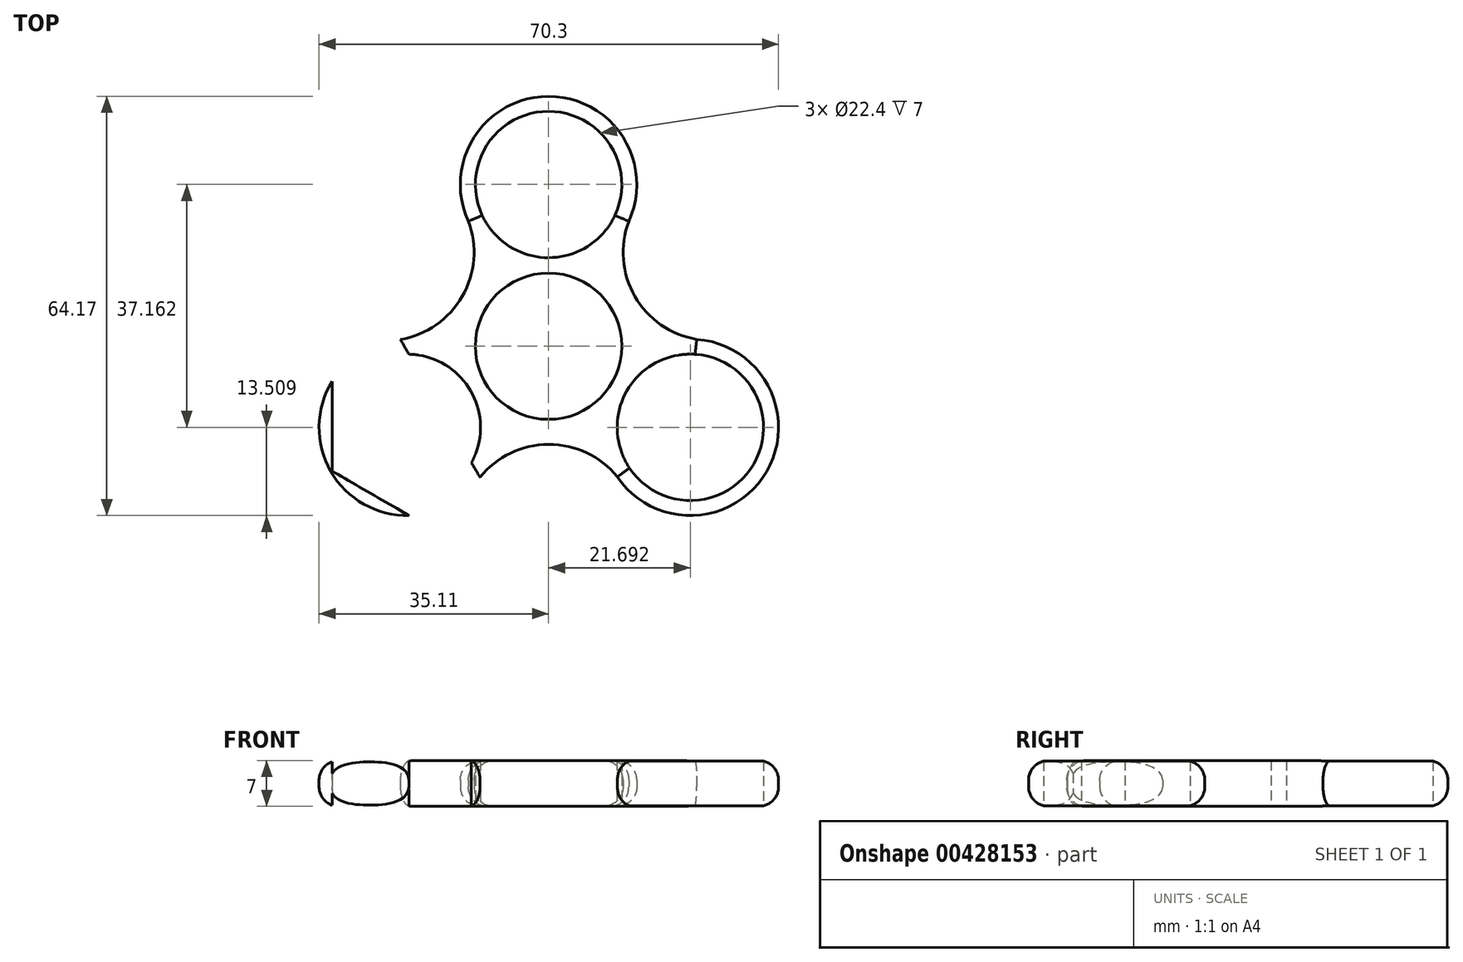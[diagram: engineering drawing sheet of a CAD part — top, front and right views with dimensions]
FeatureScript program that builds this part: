
annotation { "Feature Type Name" : "Feature", "Feature Type Description" : "" }
export const myFeature = defineFeature(function(context is Context, id is Id, definition is map)
    precondition{}
    {
        {
            var Q0;
            Q0=qCreatedBy(makeId("Top.planeOp"),FACE);
            var sketch = newSketch(context, id + "F0", { "sketchPlane" : qUnion([Q0])});
            skCircle(sketch, "E0", {"center": v(0, 0) * mm, "radius": 11.2 * mm});
            skCircle(sketch, "E1", {"center": v(0, 24.74) * mm, "radius": 11.2 * mm});
            skCircle(sketch, "E2", {"center": v(-21.6, -12.43) * mm, "radius": 11.2 * mm});
            skCircle(sketch, "E3", {"center": v(21.7, -12.42) * mm, "radius": 11.2 * mm});
            skCircle(sketch, "E4", {"center": v(21.7, -12.42) * mm, "radius": 13.5 * mm});
            skCircle(sketch, "E5", {"center": v(-21.6, -12.43) * mm, "radius": 13.5 * mm});
            skCircle(sketch, "E6", {"center": v(0, 24.74) * mm, "radius": 13.5 * mm});
            skLineSegment(sketch, "E7", {"start": v(-21.6, -12.43) * mm, "end": v(21.7, -12.42) * mm});
            skLineSegment(sketch, "E8", {"start": v(0, 24.74) * mm, "end": v(-21.6, -12.43) * mm});
            skLineSegment(sketch, "E9", {"start": v(0, 24.74) * mm, "end": v(21.7, -12.42) * mm});
            skLineSegment(sketch, "E10", {"start": v(21.7, -12.42) * mm, "end": v(-21.6, -12.43) * mm});
            skCircle(sketch, "E11.cCircle", {"center": v(0, 0) * mm, "radius": 38.24 * mm, "construction": true});
            skLineSegment(sketch, "E11.0", {"start": v(0, 38.24) * mm, "end": v(33.12, 19.12) * mm});
            skLineSegment(sketch, "E11.1", {"start": v(33.12, 19.12) * mm, "end": v(33.12, -19.12) * mm});
            skLineSegment(sketch, "E11.2", {"start": v(33.12, -19.12) * mm, "end": v(0, -38.24) * mm});
            skLineSegment(sketch, "E11.3", {"start": v(0, -38.24) * mm, "end": v(-33.12, -19.12) * mm});
            skLineSegment(sketch, "E11.4", {"start": v(-33.12, -19.12) * mm, "end": v(-33.12, 19.12) * mm});
            skLineSegment(sketch, "E11.5", {"start": v(-33.12, 19.12) * mm, "end": v(0, 38.24) * mm});
            skLineSegment(sketch, "E12", {"start": v(-33.12, 19.12) * mm, "end": v(33.12, 19.12) * mm});
            skLineSegment(sketch, "E13", {"start": v(33.12, 19.12) * mm, "end": v(0, -38.24) * mm});
            skLineSegment(sketch, "E14", {"start": v(0, -38.24) * mm, "end": v(-33.12, 19.12) * mm});
            skArc(sketch, "E15", {"start": v(12.27, 19.12) * mm, "mid": v(13.2, 7.62) * mm, "end": v(22.68, 1.04) * mm});
            skArc(sketch, "E16", {"start": v(10.53, -20) * mm, "mid": v(0, -15.02) * mm, "end": v(-10.49, -20.08) * mm});
            skArc(sketch, "E17", {"start": v(-22.67, 1.03) * mm, "mid": v(-13.2, 7.62) * mm, "end": v(-12.27, 19.12) * mm});
            skSolve(sketch);
        }
        {
            var Q0;
            Q0=makeQuery(id+"F0.imprint","IMPRINT",FACE,{"disambiguationData":[TD([[makeQuery(id+"F0.imprint","IMPRINT",EDGE,{"derivedFrom":sQuery(id+"F0.wireOp",EDGE,"E1")}),-1.0]])]});
            var Q1;
            Q1=makeQuery(id+"F0.imprint","IMPRINT",FACE,{"disambiguationData":[TD([[makeQuery(id+"F0.imprint","IMPRINT",EDGE,{"derivedFrom":sQuery(id+"F0.wireOp",EDGE,"E0")}),-1.0]])]});
            var Q2;
            Q2=makeQuery(id+"F0.imprint","IMPRINT",FACE,{"disambiguationData":[TD([[makeQuery(id+"F0.imprint","IMPRINT",EDGE,{"derivedFrom":sQuery(id+"F0.wireOp",EDGE,"E3")}),-1.0]])]});
            var Q3;
            Q3=makeQuery(id+"F0.imprint","IMPRINT",FACE,{"disambiguationData":[TD([[makeQuery(id+"F0.imprint","IMPRINT",EDGE,{"derivedFrom":sQuery(id+"F0.wireOp",EDGE,"E2")}),-1.0]])]});
            var Q4;
            {var subQ0=sQuery(id+"F0.wireOp",EDGE,"E17");Q4=makeQuery(id+"F0.imprint","IMPRINT",FACE,{"disambiguationData":[TD([[makeQuery(id+"F0.imprint","IMPRINT",EDGE,{"derivedFrom":subQ0}),-1.0]])]});}
            var Q5;
            {var subQ5=sQuery(id+"F0.wireOp",EDGE,"E12");var subQ9=sQuery(id+"F0.wireOp",EDGE,"E1");var subQ10=makeQuery(id+"F0.imprint","INTERSECT",VERTEX,{"disambiguationData":[OD(0.0)],"derivedFrom":[subQ9,subQ5]});Q5=makeQuery(id+"F0.imprint","IMPRINT",FACE,{"disambiguationData":[TD([[makeQuery(id+"F0.imprint","IMPRINT",EDGE,{"disambiguationData":[TD([[subQ10,1.0]])],"derivedFrom":subQ9}),-1.0]])]});}
            var Q6;
            {var subQ0=sQuery(id+"F0.wireOp",EDGE,"E11.5");var subQ1=sQuery(id+"F0.wireOp",EDGE,"E6");var subQ3=makeQuery(id+"F0.imprint","INTERSECT",VERTEX,{"derivedFrom":[subQ1,subQ0]});Q6=makeQuery(id+"F0.imprint","IMPRINT",FACE,{"disambiguationData":[TD([[makeQuery(id+"F0.imprint","IMPRINT",EDGE,{"disambiguationData":[TD([[subQ3,1.0]])],"derivedFrom":subQ1}),1.0]])]});}
            var Q7;
            {var subQ0=sQuery(id+"F0.wireOp",EDGE,"E11.0");var subQ1=sQuery(id+"F0.wireOp",EDGE,"E6");var subQ3=makeQuery(id+"F0.imprint","INTERSECT",VERTEX,{"derivedFrom":[subQ1,subQ0]});Q7=makeQuery(id+"F0.imprint","IMPRINT",FACE,{"disambiguationData":[TD([[makeQuery(id+"F0.imprint","IMPRINT",EDGE,{"disambiguationData":[TD([[subQ3,-1.0]])],"derivedFrom":subQ1}),1.0]])]});}
            var Q8;
            {var subQ5=sQuery(id+"F0.wireOp",EDGE,"E13");var subQ6=sQuery(id+"F0.wireOp",EDGE,"E3");var subQ7=makeQuery(id+"F0.imprint","INTERSECT",VERTEX,{"disambiguationData":[OD(0.0)],"derivedFrom":[subQ6,subQ5]});Q8=makeQuery(id+"F0.imprint","IMPRINT",FACE,{"disambiguationData":[TD([[makeQuery(id+"F0.imprint","IMPRINT",EDGE,{"disambiguationData":[TD([[subQ7,1.0]])],"derivedFrom":subQ6}),-1.0]])]});}
            var Q9;
            {var subQ0=sQuery(id+"F0.wireOp",EDGE,"E11.1");var subQ1=sQuery(id+"F0.wireOp",EDGE,"E4");var subQ2=makeQuery(id+"F0.imprint","INTERSECT",VERTEX,{"derivedFrom":[subQ1,subQ0]});Q9=makeQuery(id+"F0.imprint","IMPRINT",FACE,{"disambiguationData":[TD([[makeQuery(id+"F0.imprint","IMPRINT",EDGE,{"disambiguationData":[TD([[subQ2,1.0]])],"derivedFrom":subQ1}),1.0]])]});}
            var Q10;
            {var subQ5=sQuery(id+"F0.wireOp",EDGE,"E14");var subQ9=sQuery(id+"F0.wireOp",EDGE,"E2");var subQ10=makeQuery(id+"F0.imprint","INTERSECT",VERTEX,{"disambiguationData":[OD(0.0)],"derivedFrom":[subQ9,subQ5]});Q10=makeQuery(id+"F0.imprint","IMPRINT",FACE,{"disambiguationData":[TD([[makeQuery(id+"F0.imprint","IMPRINT",EDGE,{"disambiguationData":[TD([[subQ10,-1.0]])],"derivedFrom":subQ9}),-1.0]])]});}
            var Q11;
            {var subQ0=sQuery(id+"F0.wireOp",EDGE,"E11.4");var subQ1=sQuery(id+"F0.wireOp",EDGE,"E5");var subQ2=makeQuery(id+"F0.imprint","INTERSECT",VERTEX,{"derivedFrom":[subQ1,subQ0]});Q11=makeQuery(id+"F0.imprint","IMPRINT",FACE,{"disambiguationData":[TD([[makeQuery(id+"F0.imprint","IMPRINT",EDGE,{"disambiguationData":[TD([[subQ2,-1.0]])],"derivedFrom":subQ1}),1.0]])]});}
            var Q12;
            {var subQ0=sQuery(id+"F0.wireOp",EDGE,"E15");Q12=makeQuery(id+"F0.imprint","IMPRINT",FACE,{"disambiguationData":[TD([[makeQuery(id+"F0.imprint","IMPRINT",EDGE,{"derivedFrom":subQ0}),-1.0]])]});}
            var Q13;
            {var subQ0=sQuery(id+"F0.wireOp",EDGE,"E16");Q13=makeQuery(id+"F0.imprint","IMPRINT",FACE,{"disambiguationData":[TD([[makeQuery(id+"F0.imprint","IMPRINT",EDGE,{"derivedFrom":subQ0}),-1.0]])]});}
            extrude(context, id + "F1", {"entities" : qUnion([Q0, Q1, Q2, Q3, Q4, Q5, Q6, Q7, Q8, Q9, Q10, Q11, Q12, Q13]), "depth" : 7 * mm, "offsetDistance" : 25 * mm});
        }
        {
            var Q0;
            Q0=makeQuery(id+"F1.opExtrude","CAP_EDGE",EDGE,{"disambiguationData":[OSD([sQuery(id+"F0.wireOp",EDGE,"E17")])],"isStart":false});
            var Q1;
            Q1=makeQuery(id+"F1.opExtrude","CAP_EDGE",EDGE,{"disambiguationData":[OSD([sQuery(id+"F0.wireOp",EDGE,"E5")])],"isStart":false});
            var Q2;
            Q2=makeQuery(id+"F1.opExtrude","CAP_EDGE",EDGE,{"disambiguationData":[OSD([sQuery(id+"F0.wireOp",EDGE,"E16")])],"isStart":false});
            var Q3;
            Q3=makeQuery(id+"F1.opExtrude","CAP_EDGE",EDGE,{"disambiguationData":[OSD([sQuery(id+"F0.wireOp",EDGE,"E4")])],"isStart":false});
            var Q4;
            Q4=makeQuery(id+"F1.opExtrude","CAP_EDGE",EDGE,{"disambiguationData":[OSD([sQuery(id+"F0.wireOp",EDGE,"E15")])],"isStart":false});
            var Q5;
            Q5=makeQuery(id+"F1.opExtrude","CAP_EDGE",EDGE,{"disambiguationData":[OSD([sQuery(id+"F0.wireOp",EDGE,"E6")])],"isStart":false});
            var Q6;
            Q6=makeQuery(id+"F1.opExtrude","CAP_EDGE",EDGE,{"disambiguationData":[OSD([sQuery(id+"F0.wireOp",EDGE,"E16")])],"isStart":true});
            var Q7;
            Q7=makeQuery(id+"F1.opExtrude","CAP_EDGE",EDGE,{"disambiguationData":[OSD([sQuery(id+"F0.wireOp",EDGE,"E5")])],"isStart":true});
            var Q8;
            Q8=makeQuery(id+"F1.opExtrude","CAP_EDGE",EDGE,{"disambiguationData":[OSD([sQuery(id+"F0.wireOp",EDGE,"E17")])],"isStart":true});
            var Q9;
            Q9=makeQuery(id+"F1.opExtrude","CAP_EDGE",EDGE,{"disambiguationData":[OSD([sQuery(id+"F0.wireOp",EDGE,"E6")])],"isStart":true});
            var Q10;
            Q10=makeQuery(id+"F1.opExtrude","CAP_EDGE",EDGE,{"disambiguationData":[OSD([sQuery(id+"F0.wireOp",EDGE,"E15")])],"isStart":true});
            var Q11;
            Q11=makeQuery(id+"F1.opExtrude","CAP_EDGE",EDGE,{"disambiguationData":[OSD([sQuery(id+"F0.wireOp",EDGE,"E4")])],"isStart":true});
            fillet(context, id + "F2", {"entities" : qUnion([Q0, Q1, Q2, Q3, Q4, Q5, Q6, Q7, Q8, Q9, Q10, Q11]), "radius" : 3 * mm, "tangentPropagation" : true, "allowEdgeOverflow" : false});
        }
    });
